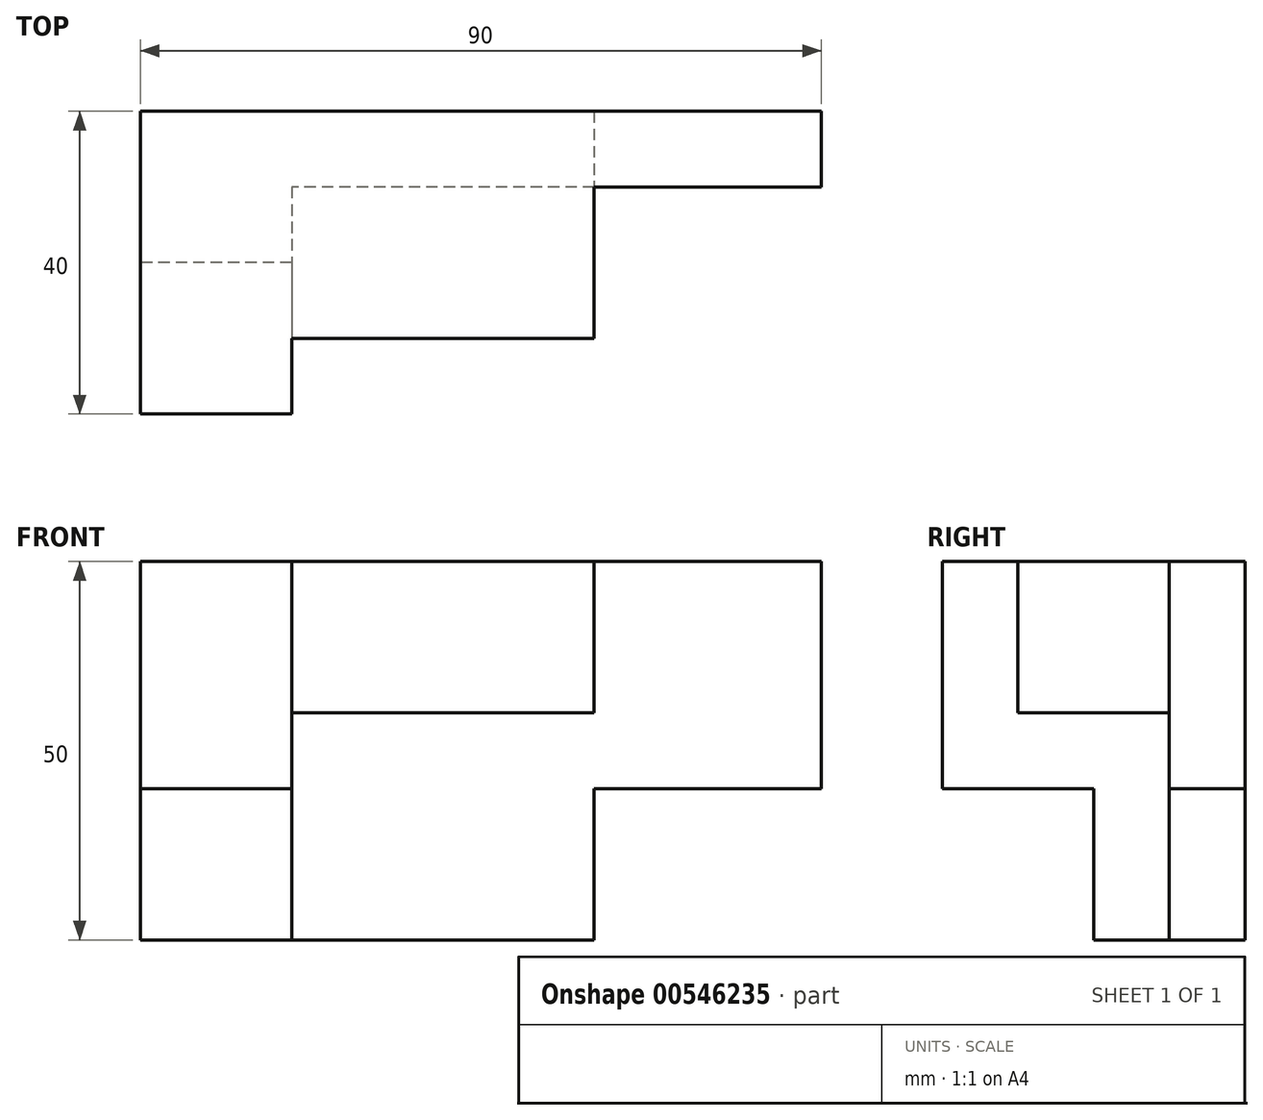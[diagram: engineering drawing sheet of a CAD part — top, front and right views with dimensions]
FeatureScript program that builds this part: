
annotation { "Feature Type Name" : "Feature", "Feature Type Description" : "" }
export const myFeature = defineFeature(function(context is Context, id is Id, definition is map)
    precondition{}
    {
        {
            var Q0;
            Q0=qCreatedBy(makeId("Front.planeOp"),FACE);
            var sketch = newSketch(context, id + "F0", { "sketchPlane" : qUnion([Q0])});
            skLineSegment(sketch, "E0.bottom", {"start": v(45, 25) * mm, "end": v(-45, 25) * mm});
            skLineSegment(sketch, "E0.top", {"start": v(45, -25) * mm, "end": v(-45, -25) * mm});
            skLineSegment(sketch, "E0.left", {"start": v(45, 25) * mm, "end": v(45, -25) * mm});
            skLineSegment(sketch, "E0.right", {"start": v(-45, 25) * mm, "end": v(-45, -25) * mm});
            skPoint(sketch, "E0.middle", {"position": v(0, 0) * mm});
            skSolve(sketch);
        }
        {
            var Q0;
            Q0=makeQuery(id+"F0.imprint","IMPRINT",FACE,{"disambiguationData":[TD([[makeQuery(id+"F0.imprint","IMPRINT",EDGE,{"derivedFrom":sQuery(id+"F0.wireOp",EDGE,"E0.bottom")}),1.0]])]});
            extrude(context, id + "F1", {"entities" : qUnion([Q0]), "depth" : 40 * mm, "offsetDistance" : 25 * mm});
        }
        {
            var Q0;
            Q0=makeQuery(id+"F1.opExtrude","CAP_FACE",FACE,{"disambiguationData":[OSD([sQuery(id+"F0.wireOp",EDGE,"E0.bottom"),sQuery(id+"F0.wireOp",EDGE,"E0.top"),sQuery(id+"F0.wireOp",EDGE,"E0.left"),sQuery(id+"F0.wireOp",EDGE,"E0.right")])],"isStart":false});
            var sketch = newSketch(context, id + "F2", { "sketchPlane" : qUnion([Q0])});
            skLineSegment(sketch, "E1", {"start": v(15, -25) * mm, "end": v(15, -5) * mm});
            skLineSegment(sketch, "E2", {"start": v(15, -5) * mm, "end": v(45, -5) * mm});
            skSolve(sketch);
        }
        {
            var Q0;
            {var subQ0=sQuery(id+"F2.wireOp",EDGE,"E1");Q0=makeQuery(id+"F2.imprint","IMPRINT",FACE,{"disambiguationData":[TD([[makeQuery(id+"F2.imprint","IMPRINT",EDGE,{"derivedFrom":subQ0}),-1.0]])]});}
            extrude(context, id + "F3", {"entities" : qUnion([Q0]), "operationType" : NewBodyOperationType.REMOVE, "endBound" : BoundingType.THROUGH_ALL, "oppositeDirection" : true, "depth" : 25 * mm, "offsetDistance" : 25 * mm});
        }
        {
            var Q0;
            Q0=makeQuery(id+"F1.opExtrude","CAP_FACE",FACE,{"disambiguationData":[OSD([sQuery(id+"F0.wireOp",EDGE,"E0.bottom"),sQuery(id+"F0.wireOp",EDGE,"E0.top"),sQuery(id+"F0.wireOp",EDGE,"E0.left"),sQuery(id+"F0.wireOp",EDGE,"E0.right")])],"isStart":false});
            var sketch = newSketch(context, id + "F4", { "sketchPlane" : qUnion([Q0])});
            skLineSegment(sketch, "E3", {"start": v(-45, -5) * mm, "end": v(-25, -5) * mm});
            skLineSegment(sketch, "E4", {"start": v(-25, -5) * mm, "end": v(-25, -25) * mm});
            skSolve(sketch);
        }
        {
            var Q0;
            {var subQ0=sQuery(id+"F4.wireOp",EDGE,"E3");Q0=makeQuery(id+"F4.imprint","IMPRINT",FACE,{"disambiguationData":[TD([[makeQuery(id+"F4.imprint","IMPRINT",EDGE,{"derivedFrom":subQ0}),-1.0]])]});}
            extrude(context, id + "F5", {"entities" : qUnion([Q0]), "operationType" : NewBodyOperationType.REMOVE, "oppositeDirection" : true, "depth" : 20 * mm, "offsetDistance" : 25 * mm});
        }
        {
            var Q0;
            Q0=makeQuery(id+"F1.opExtrude","CAP_FACE",FACE,{"disambiguationData":[OSD([sQuery(id+"F0.wireOp",EDGE,"E0.bottom"),sQuery(id+"F0.wireOp",EDGE,"E0.top"),sQuery(id+"F0.wireOp",EDGE,"E0.left"),sQuery(id+"F0.wireOp",EDGE,"E0.right")])],"isStart":false});
            var sketch = newSketch(context, id + "F6", { "sketchPlane" : qUnion([Q0])});
            skLineSegment(sketch, "E5", {"start": v(-25, 5) * mm, "end": v(15, 5) * mm});
            skLineSegment(sketch, "E6", {"start": v(15, 5) * mm, "end": v(15, 25) * mm});
            skLineSegment(sketch, "E7", {"start": v(-25, 5) * mm, "end": v(-25, 25) * mm});
            skLineSegment(sketch, "E8", {"start": v(-25, 5) * mm, "end": v(-25, -5) * mm});
            skSolve(sketch);
        }
        {
            var Q0;
            Q0=makeQuery(id+"F6.imprint","IMPRINT",FACE,{"disambiguationData":[TD([[makeQuery(id+"F6.imprint","IMPRINT",EDGE,{"derivedFrom":sQuery(id+"F6.wireOp",EDGE,"E5")}),1.0]])]});
            extrude(context, id + "F7", {"entities" : qUnion([Q0]), "operationType" : NewBodyOperationType.REMOVE, "oppositeDirection" : true, "depth" : 10 * mm, "offsetDistance" : 25 * mm});
        }
        {
            var Q0;
            Q0=makeQuery(id+"F1.opExtrude","CAP_FACE",FACE,{"disambiguationData":[OSD([sQuery(id+"F0.wireOp",EDGE,"E0.bottom"),sQuery(id+"F0.wireOp",EDGE,"E0.top"),sQuery(id+"F0.wireOp",EDGE,"E0.left"),sQuery(id+"F0.wireOp",EDGE,"E0.right")])],"isStart":false});
            var sketch = newSketch(context, id + "F8", { "sketchPlane" : qUnion([Q0])});
            skLineSegment(sketch, "E9", {"start": v(-25, 5) * mm, "end": v(-25, -5) * mm});
            skSolve(sketch);
        }
        {
            var Q0;
            Q0=makeQuery(id+"F8.imprint","IMPRINT",FACE,{"disambiguationData":[TD([[makeQuery(id+"F8.imprint","IMPRINT",EDGE,{"derivedFrom":sQuery(id+"F8.wireOp",EDGE,"E9")}),1.0]])]});
            extrude(context, id + "F9", {"entities" : qUnion([Q0]), "operationType" : NewBodyOperationType.REMOVE, "oppositeDirection" : true, "depth" : 30 * mm, "offsetDistance" : 25 * mm});
        }
    });
